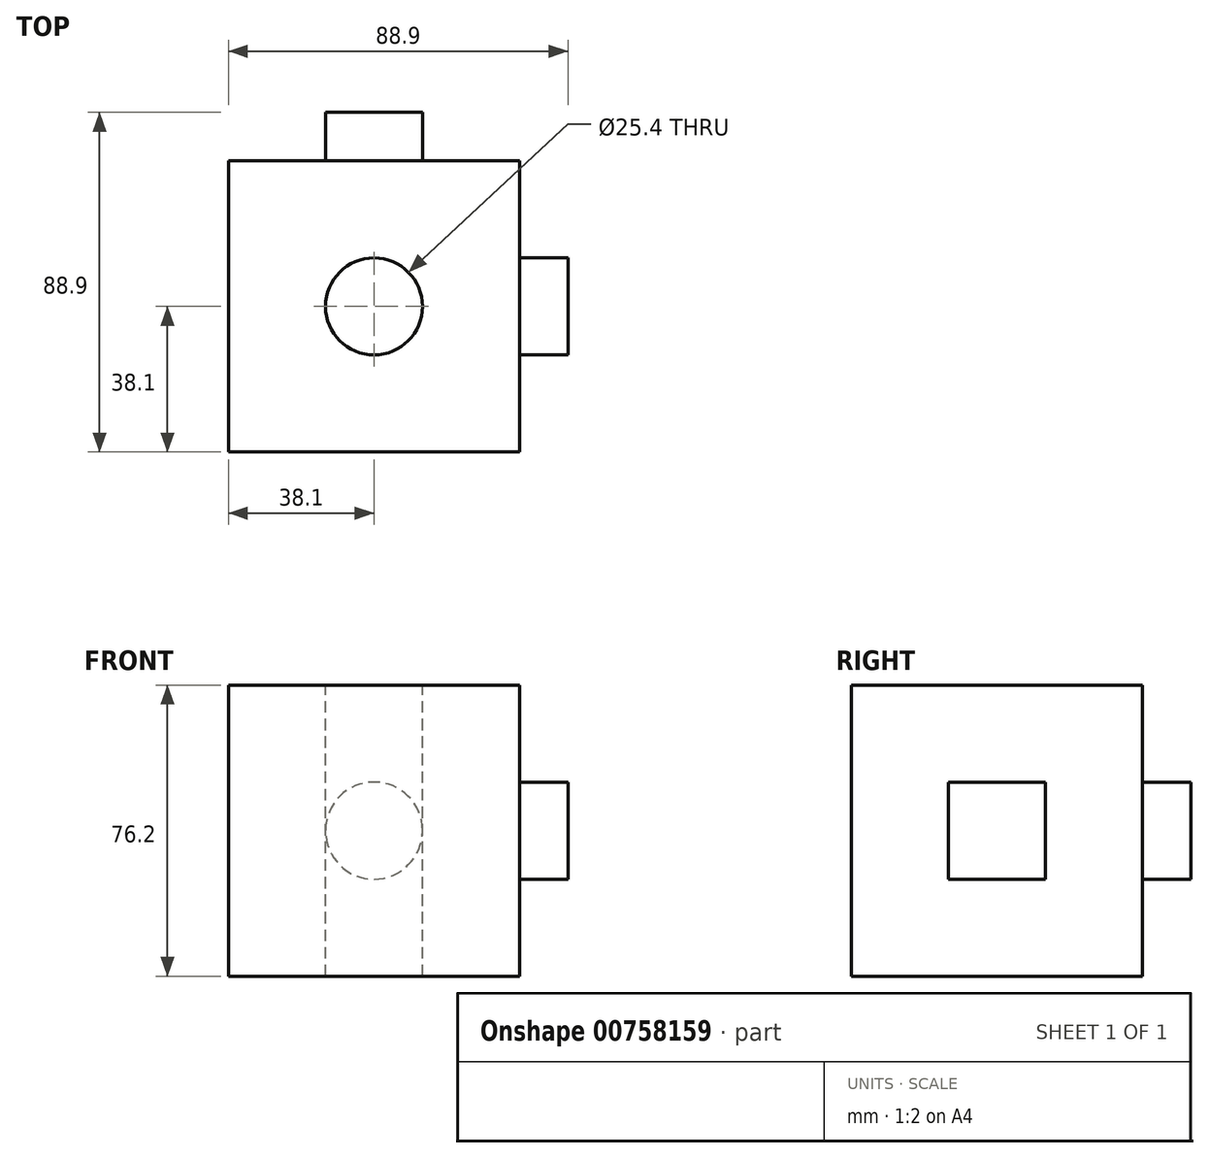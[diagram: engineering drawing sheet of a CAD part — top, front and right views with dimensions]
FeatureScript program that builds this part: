
annotation { "Feature Type Name" : "Feature", "Feature Type Description" : "" }
export const myFeature = defineFeature(function(context is Context, id is Id, definition is map)
    precondition{}
    {
        {
            var Q0;
            Q0=qCreatedBy(makeId("Front.planeOp"),FACE);
            var sketch = newSketch(context, id + "F0", { "sketchPlane" : qUnion([Q0])});
            skLineSegment(sketch, "E0.bottom", {"start": v(0, 0) * mm, "end": v(-76.2, 0) * mm});
            skLineSegment(sketch, "E0.top", {"start": v(0, -76.2) * mm, "end": v(-76.2, -76.2) * mm});
            skLineSegment(sketch, "E0.left", {"start": v(0, 0) * mm, "end": v(0, -76.2) * mm});
            skLineSegment(sketch, "E0.right", {"start": v(-76.2, 0) * mm, "end": v(-76.2, -76.2) * mm});
            skSolve(sketch);
        }
        {
            var Q0;
            Q0 = qSketchRegion(id + "F0", true);
            extrude(context, id + "F1", {"entities" : qUnion([Q0]), "depth" : 76.2 * mm, "offsetDistance" : 25.4 * mm});
        }
        {
            var Q0;
            Q0=makeQuery(id+"F1.opExtrude","SWEPT_FACE",FACE,{"disambiguationData":[OSD([sQuery(id+"F0.wireOp",EDGE,"E0.bottom")])]});
            var sketch = newSketch(context, id + "F2", { "sketchPlane" : qUnion([Q0])});
            skPoint(sketch, "E1", {"position": v(-38.1, -38.1) * mm});
            skPoint(sketch, "E1.positionSnap0", {"position": v(-38.1, 0) * mm});
            skPoint(sketch, "E1.positionSnap1", {"position": v(0, -38.1) * mm});
            skSolve(sketch);
        }
        {
            var Q0;
            Q0=sQuery(id+"F2.wireOp",VERTEX,"E1");
            var Q1;
            Q1=makeQuery(id+"F1.opExtrude","SWEPT_BODY",BODY,{"disambiguationData":[OSD([sQuery(id+"F0.wireOp",EDGE,"E0.bottom"),sQuery(id+"F0.wireOp",EDGE,"E0.top"),sQuery(id+"F0.wireOp",EDGE,"E0.left"),sQuery(id+"F0.wireOp",EDGE,"E0.right")])]});
            hole(context, id + "F3", {"style" : HoleStyle.SIMPLE, "endStyle" : HoleEndStyle.THROUGH, "holeDiameter" : 25.4 * mm, "majorDiameter" : 6.35 * mm, "isTappedThrough" : true, "tappedDepth" : 12.7 * mm, "tapClearance" : 3, "locations" : qUnion([Q0]), "scope" : qUnion([Q1])});
        }
        {
            var Q0;
            Q0=makeQuery(id+"F1.opExtrude","SWEPT_FACE",FACE,{"disambiguationData":[OSD([sQuery(id+"F0.wireOp",EDGE,"E0.left")])]});
            var sketch = newSketch(context, id + "F4", { "sketchPlane" : qUnion([Q0])});
            skPoint(sketch, "E2", {"position": v(-38.1, -38.1) * mm});
            skPoint(sketch, "E2.positionSnap0", {"position": v(0, -38.1) * mm});
            skPoint(sketch, "E2.positionSnap1", {"position": v(-38.1, 0) * mm});
            skLineSegment(sketch, "E3.bottom", {"start": v(-25.4, -25.4) * mm, "end": v(-50.8, -25.4) * mm});
            skLineSegment(sketch, "E3.top", {"start": v(-25.4, -50.8) * mm, "end": v(-50.8, -50.8) * mm});
            skLineSegment(sketch, "E3.left", {"start": v(-25.4, -25.4) * mm, "end": v(-25.4, -50.8) * mm});
            skLineSegment(sketch, "E3.right", {"start": v(-50.8, -25.4) * mm, "end": v(-50.8, -50.8) * mm});
            skSolve(sketch);
        }
        {
            var Q0;
            Q0 = qSketchRegion(id + "F4", true);
            extrude(context, id + "F5", {"entities" : qUnion([Q0]), "operationType" : NewBodyOperationType.ADD, "depth" : 12.7 * mm, "offsetDistance" : 25.4 * mm});
        }
        {
            var Q0;
            Q0=makeQuery(id+"F1.opExtrude","CAP_FACE",FACE,{"disambiguationData":[OSD([sQuery(id+"F0.wireOp",EDGE,"E0.bottom"),sQuery(id+"F0.wireOp",EDGE,"E0.top"),sQuery(id+"F0.wireOp",EDGE,"E0.left"),sQuery(id+"F0.wireOp",EDGE,"E0.right")])],"isStart":true});
            var sketch = newSketch(context, id + "F6", { "sketchPlane" : qUnion([Q0])});
            skPoint(sketch, "E4", {"position": v(38.1, -38.1) * mm});
            skPoint(sketch, "E4.positionSnap0", {"position": v(76.2, -38.1) * mm});
            skPoint(sketch, "E4.positionSnap1", {"position": v(38.1, 0) * mm});
            skCircle(sketch, "E5", {"center": v(38.1, -38.1) * mm, "radius": 12.7 * mm});
            skSolve(sketch);
        }
        {
            var Q0;
            Q0 = qSketchRegion(id + "F6", true);
            extrude(context, id + "F7", {"entities" : qUnion([Q0]), "operationType" : NewBodyOperationType.ADD, "depth" : 12.7 * mm, "offsetDistance" : 25.4 * mm});
        }
    });
